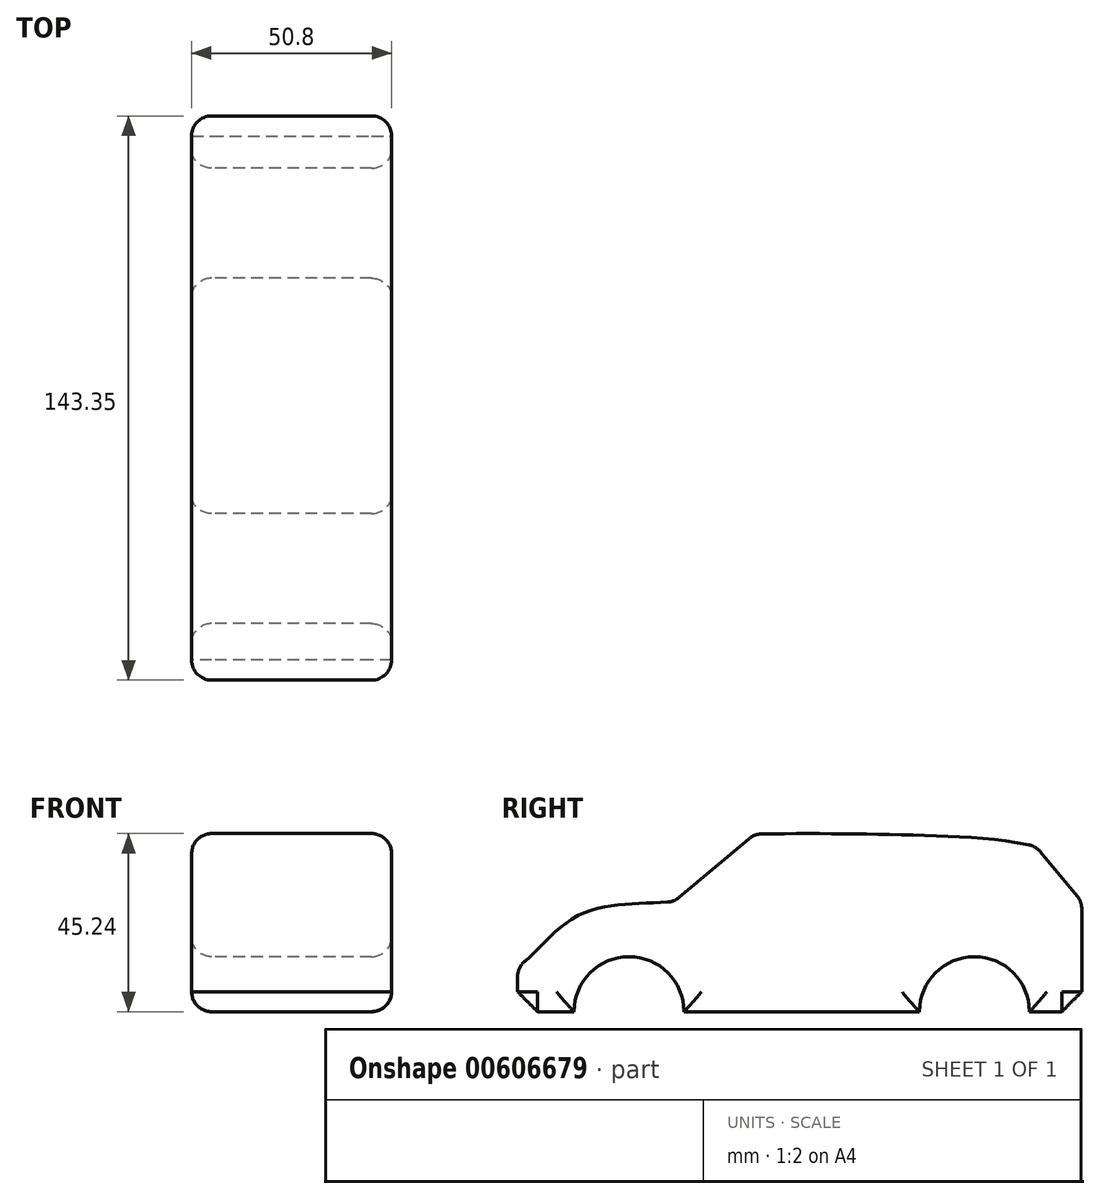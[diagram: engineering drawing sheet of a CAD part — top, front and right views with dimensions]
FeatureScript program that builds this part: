
annotation { "Feature Type Name" : "Feature", "Feature Type Description" : "" }
export const myFeature = defineFeature(function(context is Context, id is Id, definition is map)
    precondition{}
    {
        {
            var Q0;
            Q0=qCreatedBy(makeId("Right.planeOp"),FACE);
            var sketch = newSketch(context, id + "F0", { "sketchPlane" : qUnion([Q0])});
            skLineSegment(sketch, "E0", {"start": v(-61.8, -27.94) * mm, "end": v(81.56, -27.94) * mm});
            skLineSegment(sketch, "E1", {"start": v(81.56, -27.94) * mm, "end": v(81.56, 0) * mm});
            skLineSegment(sketch, "E2", {"start": v(-61.8, -27.94) * mm, "end": v(-61.8, -16.51) * mm});
            skFitSpline(sketch, "E3", {"points": [v(-61.8, -16.51) * mm, v(-46.55, -3.57) * mm, v(-22.03, 0) * mm], "startDerivative": vector(30.98, 19.75) * mm, "endDerivative": vector(48.03, 3.6) * mm});
            skLineSegment(sketch, "E4", {"start": v(-22.03, 0) * mm, "end": v(-1.69, 17.16) * mm});
            skFitSpline(sketch, "E5", {"points": [v(-1.69, 17.16) * mm, v(27.36, 17.16) * mm, v(60.36, 15.72) * mm, v(69.89, 14.05) * mm], "startDerivative": vector(72.28, 1.58) * mm, "endDerivative": vector(36.1, -7.61) * mm});
            skLineSegment(sketch, "E6", {"start": v(69.89, 14.05) * mm, "end": v(81.56, 0) * mm});
            skCircle(sketch, "E7", {"center": v(-33.48, -27.94) * mm, "radius": 13.97 * mm});
            skCircle(sketch, "E8", {"center": v(54.29, -27.94) * mm, "radius": 13.97 * mm});
            skSolve(sketch);
        }
        {
            var Q0;
            Q0=makeQuery(id+"F0.imprint","IMPRINT",FACE,{"disambiguationData":[TD([[makeQuery(id+"F0.imprint","IMPRINT",EDGE,{"derivedFrom":sQuery(id+"F0.wireOp",EDGE,"E0")}),1.0]])]});
            extrude(context, id + "F1", {"entities" : qUnion([Q0]), "depth" : 50.8 * mm, "offsetDistance" : 25.4 * mm});
        }
        {
            var Q0;
            Q0=makeQuery(id+"F1.opExtrude","SWEPT_EDGE",EDGE,{"disambiguationData":[OSD([sQuery(id+"F0.wireOp",EDGE,"E1"),sQuery(id+"F0.wireOp",EDGE,"E6")])]});
            var Q1;
            Q1=makeQuery(id+"F1.opExtrude","SWEPT_EDGE",EDGE,{"disambiguationData":[OSD([sQuery(id+"F0.wireOp",EDGE,"E5"),sQuery(id+"F0.wireOp",EDGE,"E6")])]});
            var Q2;
            Q2=makeQuery(id+"F1.opExtrude","CAP_FACE",FACE,{"disambiguationData":[OSD([sQuery(id+"F0.wireOp",EDGE,"E0"),sQuery(id+"F0.wireOp",EDGE,"E1"),sQuery(id+"F0.wireOp",EDGE,"E2"),sQuery(id+"F0.wireOp",EDGE,"E3"),sQuery(id+"F0.wireOp",EDGE,"E4"),sQuery(id+"F0.wireOp",EDGE,"E5"),sQuery(id+"F0.wireOp",EDGE,"E6")])],"isStart":false});
            var Q3;
            Q3=makeQuery(id+"F1.opExtrude","CAP_FACE",FACE,{"disambiguationData":[OSD([sQuery(id+"F0.wireOp",EDGE,"E0"),sQuery(id+"F0.wireOp",EDGE,"E1"),sQuery(id+"F0.wireOp",EDGE,"E2"),sQuery(id+"F0.wireOp",EDGE,"E3"),sQuery(id+"F0.wireOp",EDGE,"E4"),sQuery(id+"F0.wireOp",EDGE,"E5"),sQuery(id+"F0.wireOp",EDGE,"E6")])],"isStart":true});
            var Q4;
            Q4=makeQuery(id+"F1.opExtrude","SWEPT_FACE",FACE,{"disambiguationData":[OSD([sQuery(id+"F0.wireOp",EDGE,"E5")])]});
            var Q5;
            Q5=makeQuery(id+"F1.opExtrude","SWEPT_FACE",FACE,{"disambiguationData":[OSD([sQuery(id+"F0.wireOp",EDGE,"E3")])]});
            fillet(context, id + "F2", {"entities" : qUnion([Q0, Q1, Q2, Q3, Q4, Q5]), "radius" : 5.08 * mm, "tangentPropagation" : true, "allowEdgeOverflow" : false});
        }
        {
            var Q0;
            Q0=makeQuery(id+"F1.opExtrude","SWEPT_EDGE",EDGE,{"disambiguationData":[OSD([sQuery(id+"F0.wireOp",EDGE,"E0"),sQuery(id+"F0.wireOp",EDGE,"E2")])]});
            var Q1;
            Q1=makeQuery(id+"F1.opExtrude","SWEPT_EDGE",EDGE,{"disambiguationData":[OSD([sQuery(id+"F0.wireOp",EDGE,"E0"),sQuery(id+"F0.wireOp",EDGE,"E1")])]});
            var Q2;
            {var subQ0=sQuery(id+"F0.wireOp",EDGE,"E3");Q2=makeQuery(id+"F2.opFillet","BLEND_EDGE",EDGE,{"blendedFrom":[makeQuery(id+"F1.opExtrude","SWEPT_EDGE",EDGE,{"disambiguationData":[OSD([subQ0,sQuery(id+"F0.wireOp",EDGE,"E4")])]}),makeQuery(id+"F1.opExtrude","SWEPT_FACE",FACE,{"disambiguationData":[OSD([subQ0])]})],"blendedInto":[makeQuery(id+"F1.opExtrude","SWEPT_FACE",FACE,{"disambiguationData":[OSD([subQ0])]})]});}
            chamfer(context, id + "F3", {"entities" : qUnion([Q0, Q1, Q2]), "width" : 5.08 * mm, "tangentPropagation" : true});
        }
    });
